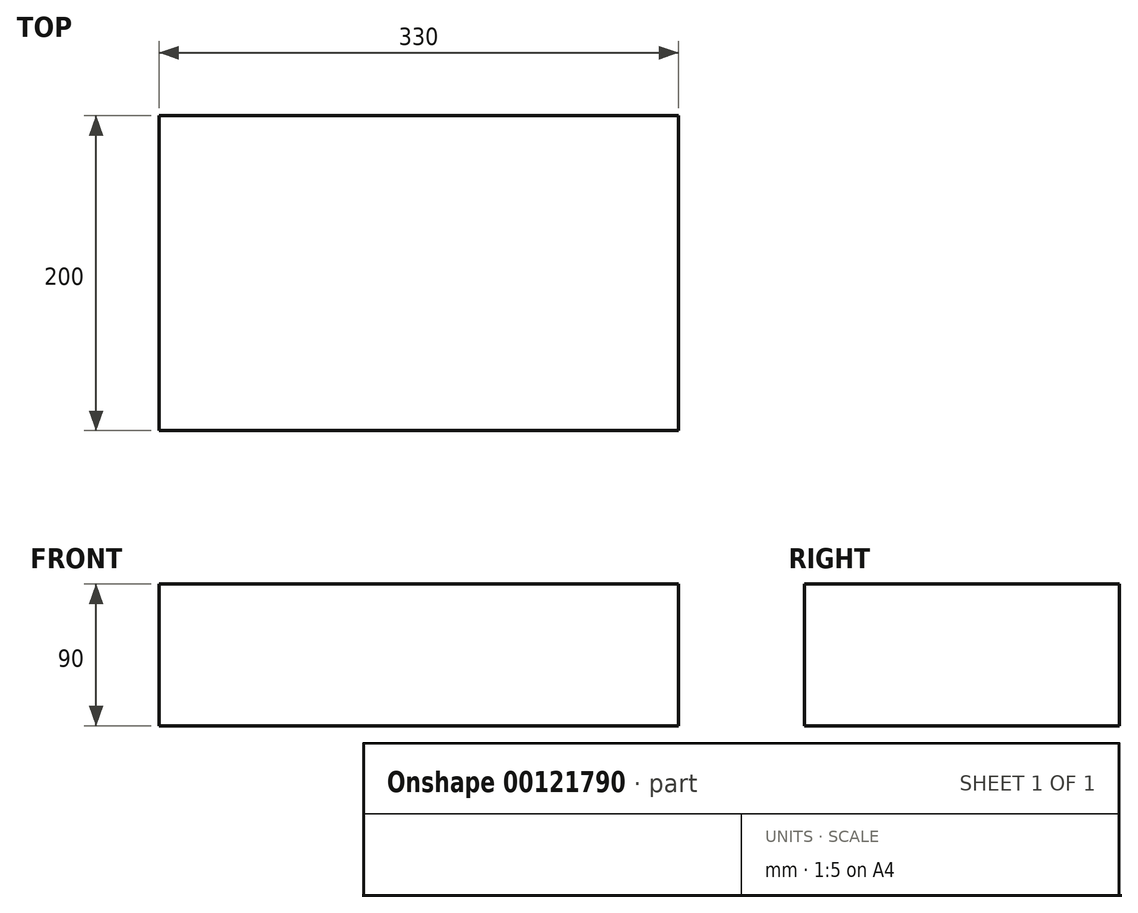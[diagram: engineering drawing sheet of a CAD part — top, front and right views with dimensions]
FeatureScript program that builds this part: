
annotation { "Feature Type Name" : "Feature", "Feature Type Description" : "" }
export const myFeature = defineFeature(function(context is Context, id is Id, definition is map)
    precondition{}
    {
        {
            var Q0;
            Q0=qCreatedBy(makeId("Top.planeOp"),FACE);
            var sketch = newSketch(context, id + "F0", { "sketchPlane" : qUnion([Q0])});
            skLineSegment(sketch, "E0", {"start": v(-290.86, -74.19) * mm, "end": v(289.44, -74.19) * mm});
            skLineSegment(sketch, "E1", {"start": v(289.44, -74.19) * mm, "end": v(289.44, -39.19) * mm});
            skLineSegment(sketch, "E2", {"start": v(289.44, -39.19) * mm, "end": v(-290.56, -39.19) * mm});
            skLineSegment(sketch, "E3", {"start": v(-290.56, -39.19) * mm, "end": v(-290.86, -74.19) * mm});
            skLineSegment(sketch, "E4", {"start": v(-166.37, -134.19) * mm, "end": v(163.63, -134.19) * mm});
            skLineSegment(sketch, "E5", {"start": v(-166.37, -134.19) * mm, "end": v(-166.37, 65.81) * mm});
            skLineSegment(sketch, "E6", {"start": v(-166.37, 65.81) * mm, "end": v(163.63, 65.81) * mm});
            skLineSegment(sketch, "E7", {"start": v(163.63, 65.81) * mm, "end": v(163.63, -134.19) * mm});
            skSolve(sketch);
        }
        {
            var Q0;
            {var subQ5=sQuery(id+"F0.wireOp",EDGE,"E4");Q0=makeQuery(id+"F0.imprint","IMPRINT",FACE,{"disambiguationData":[TD([[makeQuery(id+"F0.imprint","IMPRINT",EDGE,{"derivedFrom":subQ5}),1.0]])]});}
            var Q1;
            {var subQ0=sQuery(id+"F0.wireOp",EDGE,"E5");var subQ1=sQuery(id+"F0.wireOp",EDGE,"E0");var subQ2=makeQuery(id+"F0.imprint","INTERSECT",VERTEX,{"derivedFrom":[subQ1,subQ0]});Q1=makeQuery(id+"F0.imprint","IMPRINT",FACE,{"disambiguationData":[TD([[makeQuery(id+"F0.imprint","IMPRINT",EDGE,{"disambiguationData":[TD([[subQ2,-1.0]])],"derivedFrom":subQ1}),1.0]])]});}
            var Q2;
            {var subQ5=sQuery(id+"F0.wireOp",EDGE,"E6");Q2=makeQuery(id+"F0.imprint","IMPRINT",FACE,{"disambiguationData":[TD([[makeQuery(id+"F0.imprint","IMPRINT",EDGE,{"derivedFrom":subQ5}),-1.0]])]});}
            extrude(context, id + "F1", {"entities" : qUnion([Q0, Q1, Q2]), "depth" : 90 * mm});
        }
    });
